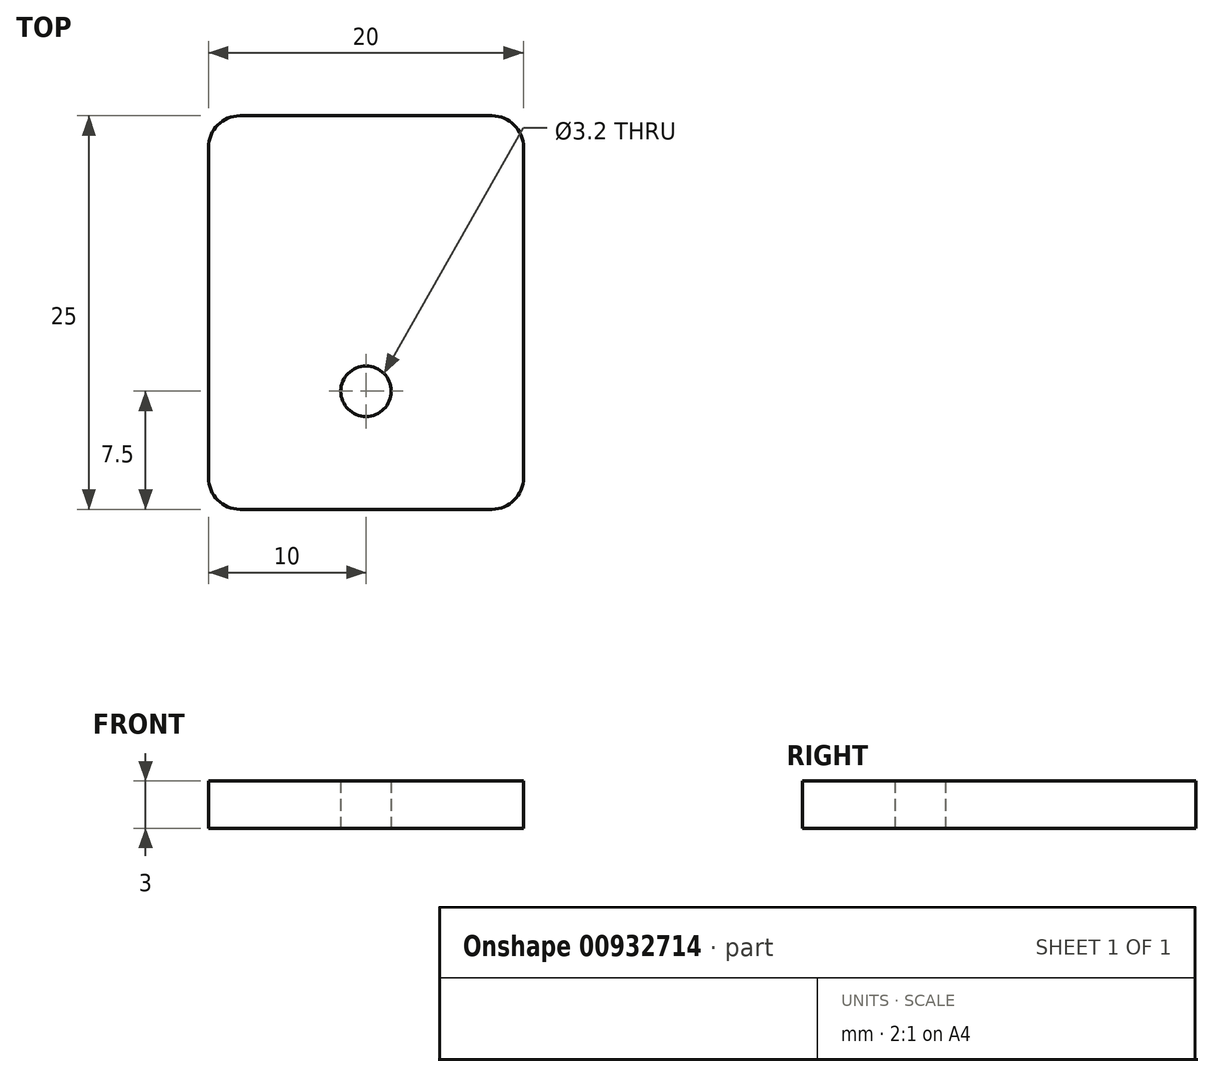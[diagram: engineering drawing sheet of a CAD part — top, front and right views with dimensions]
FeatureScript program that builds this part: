
annotation { "Feature Type Name" : "Feature", "Feature Type Description" : "" }
export const myFeature = defineFeature(function(context is Context, id is Id, definition is map)
    precondition{}
    {
        {
            var Q0;
            Q0=qCreatedBy(makeId("Top.planeOp"),FACE);
            var sketch = newSketch(context, id + "F0", { "sketchPlane" : qUnion([Q0])});
            skCircle(sketch, "E0", {"center": v(0, 0) * mm, "radius": 1.6 * mm});
            skLineSegment(sketch, "E1.bottom", {"start": v(-10, 17.5) * mm, "end": v(10, 17.5) * mm});
            skLineSegment(sketch, "E1.top", {"start": v(-10, -7.5) * mm, "end": v(10, -7.5) * mm});
            skLineSegment(sketch, "E1.left", {"start": v(-10, 17.5) * mm, "end": v(-10, -7.5) * mm});
            skLineSegment(sketch, "E1.right", {"start": v(10, 17.5) * mm, "end": v(10, -7.5) * mm});
            skLineSegment(sketch, "E2", {"start": v(0, -7.5) * mm, "end": v(0, 0) * mm, "construction": true});
            skSolve(sketch);
        }
        {
            var Q0;
            Q0=makeQuery(id+"F0.imprint","IMPRINT",FACE,{"disambiguationData":[TD([[makeQuery(id+"F0.imprint","IMPRINT",EDGE,{"derivedFrom":sQuery(id+"F0.wireOp",EDGE,"E0")}),-1.0]])]});
            extrude(context, id + "F1", {"entities" : qUnion([Q0]), "depth" : 3 * mm, "offsetDistance" : 25 * mm});
        }
        {
            var Q0;
            Q0=makeQuery(id+"F1.opExtrude","SWEPT_EDGE",EDGE,{"disambiguationData":[OSD([sQuery(id+"F0.wireOp",EDGE,"E1.top"),sQuery(id+"F0.wireOp",EDGE,"E1.left")])]});
            var Q1;
            Q1=makeQuery(id+"F1.opExtrude","SWEPT_EDGE",EDGE,{"disambiguationData":[OSD([sQuery(id+"F0.wireOp",EDGE,"E1.top"),sQuery(id+"F0.wireOp",EDGE,"E1.right")])]});
            var Q2;
            Q2=makeQuery(id+"F1.opExtrude","SWEPT_EDGE",EDGE,{"disambiguationData":[OSD([sQuery(id+"F0.wireOp",EDGE,"E1.bottom"),sQuery(id+"F0.wireOp",EDGE,"E1.left")])]});
            var Q3;
            Q3=makeQuery(id+"F1.opExtrude","SWEPT_EDGE",EDGE,{"disambiguationData":[OSD([sQuery(id+"F0.wireOp",EDGE,"E1.bottom"),sQuery(id+"F0.wireOp",EDGE,"E1.right")])]});
            fillet(context, id + "F2", {"entities" : qUnion([Q0, Q1, Q2, Q3]), "radius" : 2 * mm, "tangentPropagation" : true, "allowEdgeOverflow" : false});
        }
    });
